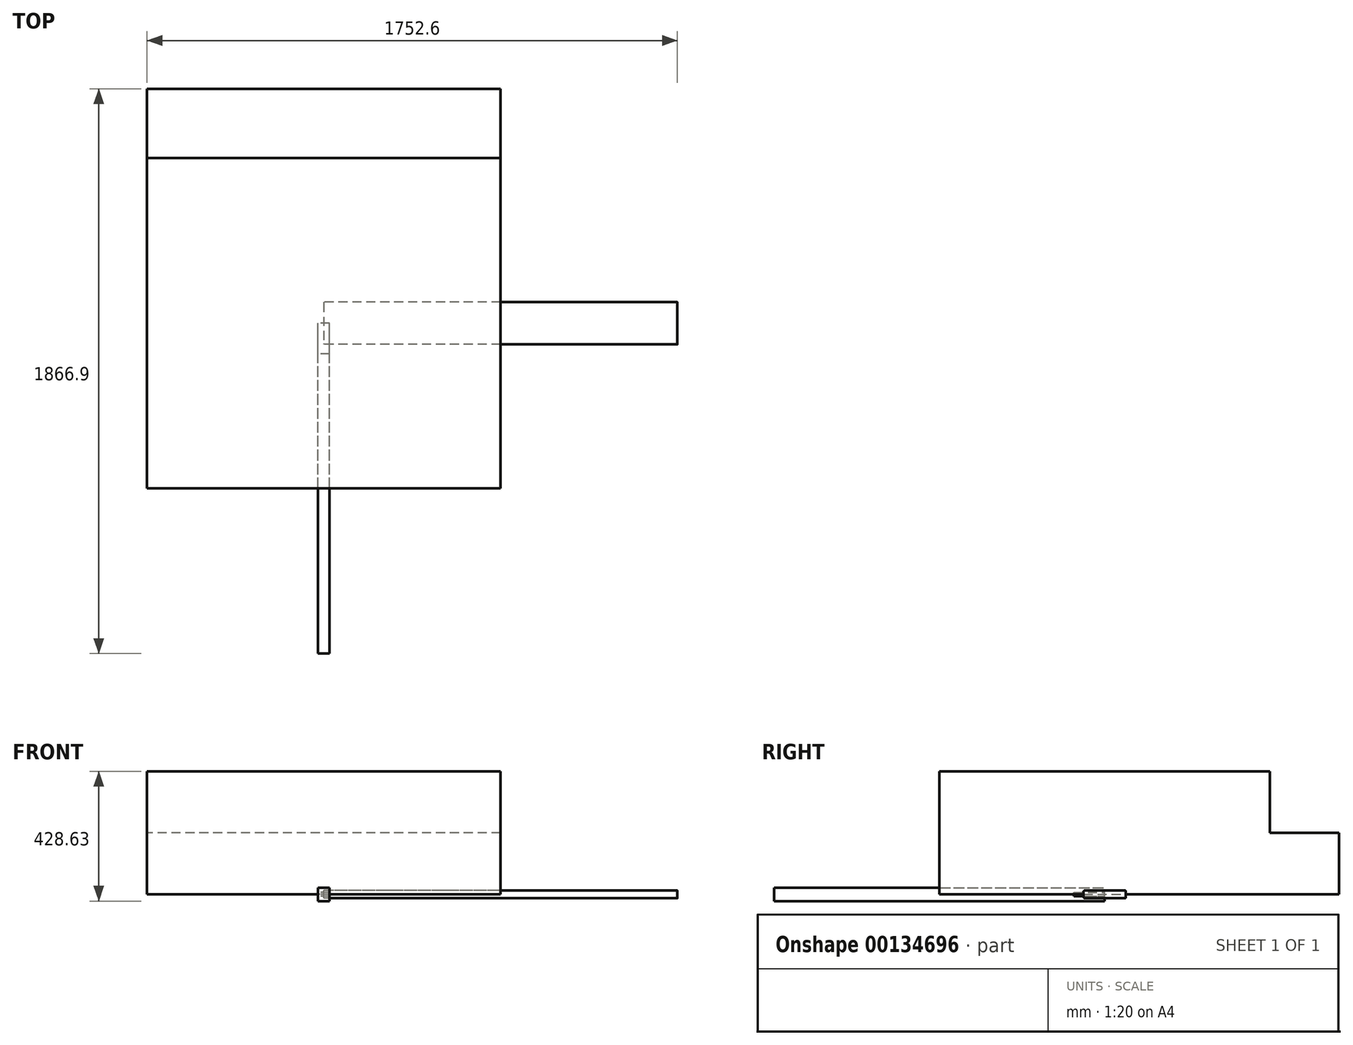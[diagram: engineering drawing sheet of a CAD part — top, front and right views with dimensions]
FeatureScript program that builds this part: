
annotation { "Feature Type Name" : "Feature", "Feature Type Description" : "" }
export const myFeature = defineFeature(function(context is Context, id is Id, definition is map)
    precondition{}
    {
        {
            var Q0;
            Q0=qCreatedBy(makeId("Front.planeOp"),FACE);
            var sketch = newSketch(context, id + "F0", { "sketchPlane" : qUnion([Q0])});
            skLineSegment(sketch, "E0.bottom", {"start": v(19.05, -6.35) * mm, "end": v(-19.05, -6.35) * mm});
            skLineSegment(sketch, "E0.top", {"start": v(19.05, 6.35) * mm, "end": v(-19.05, 6.35) * mm});
            skLineSegment(sketch, "E0.left", {"start": v(19.05, -6.35) * mm, "end": v(19.05, 6.35) * mm});
            skLineSegment(sketch, "E0.right", {"start": v(-19.05, -6.35) * mm, "end": v(-19.05, 6.35) * mm});
            skPoint(sketch, "E0.middle", {"position": v(0, 0) * mm});
            skSolve(sketch);
        }
        {
            var Q0;
            Q0=makeQuery(id+"F0.imprint","IMPRINT",FACE,{"disambiguationData":[TD([[makeQuery(id+"F0.imprint","IMPRINT",EDGE,{"derivedFrom":sQuery(id+"F0.wireOp",EDGE,"E0.bottom")}),-1.0]])]});
            extrude(context, id + "F1", {"entities" : qUnion([Q0]), "depth" : 101.6 * mm});
        }
        {
            var Q0;
            Q0=qCreatedBy(makeId("Front.planeOp"),FACE);
            var sketch = newSketch(context, id + "F2", { "sketchPlane" : qUnion([Q0])});
            skLineSegment(sketch, "E1.bottom", {"start": v(19.05, -22.23) * mm, "end": v(-19.05, -22.23) * mm});
            skLineSegment(sketch, "E1.top", {"start": v(19.05, 22.23) * mm, "end": v(-19.05, 22.22) * mm});
            skLineSegment(sketch, "E1.left", {"start": v(19.05, -22.23) * mm, "end": v(19.05, 22.23) * mm});
            skLineSegment(sketch, "E1.right", {"start": v(-19.05, -22.23) * mm, "end": v(-19.05, 22.23) * mm});
            skPoint(sketch, "E1.middle", {"position": v(0, 0) * mm});
            skSolve(sketch);
        }
        {
            var Q0;
            Q0 = qSketchRegion(id + "F2", true);
            extrude(context, id + "F3", {"entities" : qUnion([Q0]), "depth" : 1092.2 * mm});
        }
        {
            var Q0;
            Q0=qCreatedBy(makeId("Right.planeOp"),FACE);
            var sketch = newSketch(context, id + "F4", { "sketchPlane" : qUnion([Q0])});
            skLineSegment(sketch, "E2.bottom", {"start": v(66.68, -12.7) * mm, "end": v(-66.68, -12.7) * mm});
            skLineSegment(sketch, "E2.top", {"start": v(66.68, 12.7) * mm, "end": v(-66.68, 12.7) * mm});
            skLineSegment(sketch, "E2.left", {"start": v(69.85, -9.52) * mm, "end": v(69.85, 9.53) * mm});
            skLineSegment(sketch, "E2.right", {"start": v(-69.85, -9.53) * mm, "end": v(-69.85, 9.52) * mm});
            skPoint(sketch, "E2.middle", {"position": v(0, 0) * mm});
            skPoint(sketch, "E3.visualSharp", {"position": v(-69.85, 12.7) * mm});
            skArc(sketch, "E3.filletArc", {"start": v(-66.68, 12.7) * mm, "mid": v(-68.92, 11.77) * mm, "end": v(-69.85, 9.52) * mm});
            skPoint(sketch, "E4.visualSharp", {"position": v(69.85, 12.7) * mm});
            skArc(sketch, "E4.filletArc", {"start": v(69.85, 9.53) * mm, "mid": v(68.92, 11.77) * mm, "end": v(66.68, 12.7) * mm});
            skPoint(sketch, "E5.visualSharp", {"position": v(69.85, -12.7) * mm});
            skArc(sketch, "E5.filletArc", {"start": v(66.68, -12.7) * mm, "mid": v(68.92, -11.77) * mm, "end": v(69.85, -9.52) * mm});
            skPoint(sketch, "E6.visualSharp", {"position": v(-69.85, -12.7) * mm});
            skArc(sketch, "E6.filletArc", {"start": v(-69.85, -9.53) * mm, "mid": v(-68.92, -11.77) * mm, "end": v(-66.68, -12.7) * mm});
            skSolve(sketch);
        }
        {
            var Q0;
            Q0=makeQuery(id+"F4.imprint","IMPRINT",FACE,{"disambiguationData":[TD([[makeQuery(id+"F4.imprint","IMPRINT",EDGE,{"derivedFrom":sQuery(id+"F4.wireOp",EDGE,"E2.bottom")}),-1.0]])]});
            extrude(context, id + "F5", {"entities" : qUnion([Q0]), "depth" : 1168.4 * mm});
        }
        {
            var Q0;
            Q0=qCreatedBy(makeId("Top.planeOp"),FACE);
            var sketch = newSketch(context, id + "F6", { "sketchPlane" : qUnion([Q0])});
            skLineSegment(sketch, "E7.bottom", {"start": v(584.2, -546.1) * mm, "end": v(-584.2, -546.1) * mm});
            skLineSegment(sketch, "E7.top", {"start": v(584.2, 546.1) * mm, "end": v(-584.2, 546.1) * mm});
            skLineSegment(sketch, "E7.left", {"start": v(584.2, -546.1) * mm, "end": v(584.2, 546.1) * mm});
            skLineSegment(sketch, "E7.right", {"start": v(-584.2, -546.1) * mm, "end": v(-584.2, 546.1) * mm});
            skPoint(sketch, "E7.middle", {"position": v(0, 0) * mm});
            skSolve(sketch);
        }
        {
            var Q0;
            Q0=makeQuery(id+"F6.imprint","IMPRINT",FACE,{"disambiguationData":[TD([[makeQuery(id+"F6.imprint","IMPRINT",EDGE,{"derivedFrom":sQuery(id+"F6.wireOp",EDGE,"E7.bottom")}),-1.0]])]});
            extrude(context, id + "F7", {"entities" : qUnion([Q0]), "depth" : 406.4 * mm});
        }
        {
            var Q0;
            Q0=makeQuery(id+"F7.opExtrude","SWEPT_FACE",FACE,{"disambiguationData":[OSD([sQuery(id+"F6.wireOp",EDGE,"E7.top")])]});
            var sketch = newSketch(context, id + "F8", { "sketchPlane" : qUnion([Q0])});
            skLineSegment(sketch, "E8.bottom", {"start": v(-584.2, 0) * mm, "end": v(584.2, 0) * mm});
            skLineSegment(sketch, "E8.top", {"start": v(-584.2, 203.2) * mm, "end": v(584.2, 203.2) * mm});
            skLineSegment(sketch, "E8.left", {"start": v(-584.2, 0) * mm, "end": v(-584.2, 203.2) * mm});
            skLineSegment(sketch, "E8.right", {"start": v(584.2, 0) * mm, "end": v(584.2, 203.2) * mm});
            skSolve(sketch);
        }
        {
            var Q0;
            Q0 = qSketchRegion(id + "F8", true);
            extrude(context, id + "F9", {"entities" : qUnion([Q0]), "operationType" : NewBodyOperationType.ADD, "depth" : 228.6 * mm});
        }
    });
